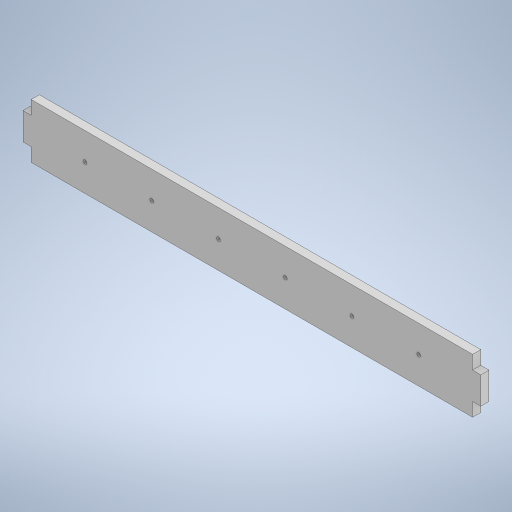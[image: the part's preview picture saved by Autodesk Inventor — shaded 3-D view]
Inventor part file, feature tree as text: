
AUTODESK INVENTOR PART (.ipt)
format: ipt  version: 2023 (Build 270158000, 158)  size: 259,072 bytes
history: native  units: mm
features: extrude x1, sketch x1
ambient origin geometry x8: Origin, YZ Plane, XZ Plane, XY Plane, X Axis, Y Axis, Z Axis, Center Point
bodies: Body1 (feature_tree)
feature tree (2):
  extrude  "Extrusion2"  Depth=20.0mm
  sketch  "Sketch1"  dims[d13=162.0mm d14=20.0mm d15=24.5mm d16=24.5mm d17=3.0mm d18=10.0mm d19=2.7mm d20=2.7mm d21=3.0mm d22=10.0mm d25=49.0mm d26=49.0mm d27=2.7mm d28=2.7mm d29=49.0mm d30=49.0mm d31=2.7mm d32=2.7mm d33=6.0mm d34=0.0mm d35=0.5mm d36=0.872665mm]
